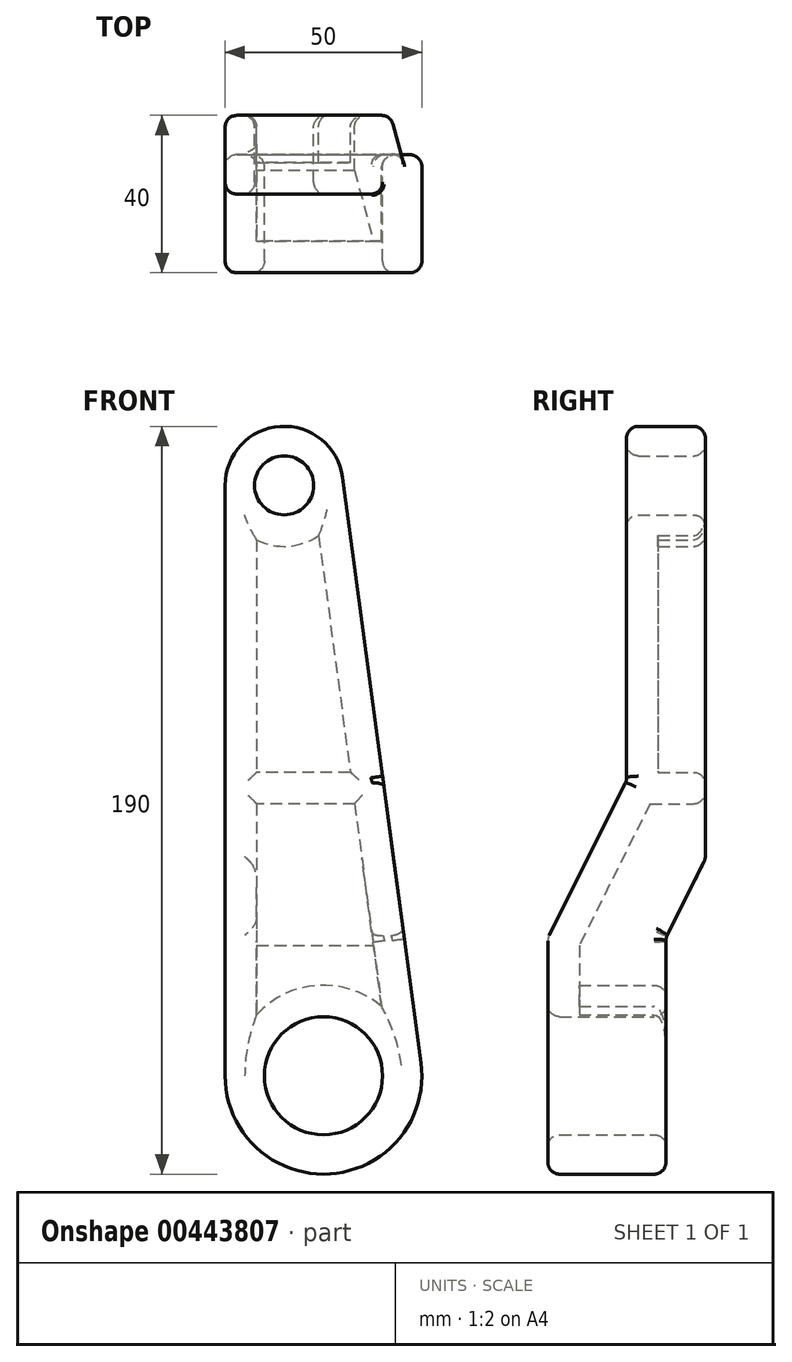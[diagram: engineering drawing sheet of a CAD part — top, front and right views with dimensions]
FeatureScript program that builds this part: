
annotation { "Feature Type Name" : "Feature", "Feature Type Description" : "" }
export const myFeature = defineFeature(function(context is Context, id is Id, definition is map)
    precondition{}
    {
        {
            var Q0;
            Q0=qCreatedBy(makeId("Front.planeOp"),FACE);
            var sketch = newSketch(context, id + "F0", { "sketchPlane" : qUnion([Q0])});
            skArc(sketch, "E0", {"start": v(-25, 0) * mm, "mid": v(1.66, -24.94) * mm, "end": v(24.78, 3.32) * mm});
            skArc(sketch, "E1", {"start": v(4.87, 152) * mm, "mid": v(-11, 164.97) * mm, "end": v(-25, 150) * mm});
            skLineSegment(sketch, "E2", {"start": v(-25, 150) * mm, "end": v(-25, 0) * mm});
            skLineSegment(sketch, "E3", {"start": v(4.87, 152) * mm, "end": v(24.78, 3.32) * mm});
            skSolve(sketch);
        }
        {
            var Q0;
            Q0 = qSketchRegion(id + "F0", true);
            extrude(context, id + "F1", {"entities" : qUnion([Q0]), "depth" : 40 * mm});
        }
        {
            var Q0;
            Q0=qCreatedBy(makeId("Right.planeOp"),FACE);
            var sketch = newSketch(context, id + "F2", { "sketchPlane" : qUnion([Q0])});
            skLineSegment(sketch, "E4", {"start": v(0, 0) * mm, "end": v(0, -25.94) * mm});
            skLineSegment(sketch, "E5", {"start": v(-10, -25.94) * mm, "end": v(-10, 35) * mm});
            skLineSegment(sketch, "E6", {"start": v(-10, 35) * mm, "end": v(0, 55) * mm});
            skLineSegment(sketch, "E7", {"start": v(0, 55) * mm, "end": v(0, -25.94) * mm});
            skLineSegment(sketch, "E8", {"start": v(-40, 35) * mm, "end": v(-40, 165.97) * mm});
            skLineSegment(sketch, "E9", {"start": v(-20, 165.97) * mm, "end": v(-20, 75) * mm});
            skLineSegment(sketch, "E10", {"start": v(-20, 75) * mm, "end": v(-40, 35) * mm});
            skLineSegment(sketch, "E11", {"start": v(0, -25.94) * mm, "end": v(-10, -25.94) * mm});
            skLineSegment(sketch, "E12", {"start": v(-20, 165.97) * mm, "end": v(-40, 165.97) * mm});
            skSolve(sketch);
        }
        {
            var Q0;
            Q0 = qSketchRegion(id + "F2", true);
            extrude(context, id + "F3", {"entities" : qUnion([Q0]), "operationType" : NewBodyOperationType.REMOVE, "endBound" : BoundingType.THROUGH_ALL, "oppositeDirection" : true, "depth" : 25 * mm, "hasSecondDirection" : true, "secondDirectionBound" : SecondDirectionBoundingType.THROUGH_ALL, "secondDirectionOppositeDirection" : false, "secondDirectionDepth" : 25 * mm});
        }
        {
            var Q0;
            Q0=makeQuery(id+"F1.opExtrude","CAP_FACE",FACE,{"disambiguationData":[OSD([sQuery(id+"F0.wireOp",EDGE,"E0"),sQuery(id+"F0.wireOp",EDGE,"E1"),sQuery(id+"F0.wireOp",EDGE,"E2"),sQuery(id+"F0.wireOp",EDGE,"E3")])],"isStart":true});
            var sketch = newSketch(context, id + "F4", { "sketchPlane" : qUnion([Q0])});
            skCircle(sketch, "E13", {"center": v(10, 150) * mm, "radius": 7.5 * mm});
            skCircle(sketch, "E14", {"center": v(0, 0) * mm, "radius": 15 * mm});
            skSolve(sketch);
        }
        {
            var Q0;
            Q0=makeQuery(id+"F4.imprint","IMPRINT",FACE,{"disambiguationData":[TD([[makeQuery(id+"F4.imprint","IMPRINT",EDGE,{"derivedFrom":sQuery(id+"F4.wireOp",EDGE,"E13")}),1.0]])]});
            var Q1;
            Q1=makeQuery(id+"F4.imprint","IMPRINT",FACE,{"disambiguationData":[TD([[makeQuery(id+"F4.imprint","IMPRINT",EDGE,{"derivedFrom":sQuery(id+"F4.wireOp",EDGE,"E14")}),1.0]])]});
            extrude(context, id + "F5", {"entities" : qUnion([Q0, Q1]), "operationType" : NewBodyOperationType.REMOVE, "endBound" : BoundingType.THROUGH_ALL, "oppositeDirection" : true, "depth" : 25 * mm});
        }
        {
            var Q0;
            Q0=makeQuery(id+"F1.opExtrude","CAP_FACE",FACE,{"disambiguationData":[OSD([sQuery(id+"F0.wireOp",EDGE,"E0"),sQuery(id+"F0.wireOp",EDGE,"E1"),sQuery(id+"F0.wireOp",EDGE,"E2"),sQuery(id+"F0.wireOp",EDGE,"E3")])],"isStart":true});
            var Q1;
            Q1=makeQuery(id+"F3.boolean.opBoolean","COPY",FACE,{"derivedFrom":makeQuery(id+"F3.opExtrude","SWEPT_FACE",FACE,{"disambiguationData":[OSD([sQuery(id+"F2.wireOp",EDGE,"E6")])]})});
            var Q2;
            Q2=makeQuery(id+"F3.boolean.opBoolean","COPY",FACE,{"derivedFrom":makeQuery(id+"F3.opExtrude","SWEPT_FACE",FACE,{"disambiguationData":[OSD([sQuery(id+"F2.wireOp",EDGE,"E5")])]})});
            shell(context, id + "F6", {"entities" : qUnion([Q0, Q1, Q2]), "thickness" : 8 * mm});
        }
        {
            var Q0;
            Q0=makeQuery(id+"F1.opExtrude","CAP_FACE",FACE,{"disambiguationData":[OSD([sQuery(id+"F0.wireOp",EDGE,"E0"),sQuery(id+"F0.wireOp",EDGE,"E1"),sQuery(id+"F0.wireOp",EDGE,"E2"),sQuery(id+"F0.wireOp",EDGE,"E3")])],"isStart":true});
            var sketch = newSketch(context, id + "F7", { "sketchPlane" : qUnion([Q0])});
            skLineSegment(sketch, "E15", {"start": v(-6.82, 77.11) * mm, "end": v(17, 77.11) * mm});
            skLineSegment(sketch, "E16", {"start": v(-7.9, 69.11) * mm, "end": v(17, 69.11) * mm});
            skLineSegment(sketch, "E17.0", {"start": v(1.23, 137.22) * mm, "end": v(-9.79, 55) * mm});
            skLineSegment(sketch, "E18.0", {"start": v(17, 136.17) * mm, "end": v(17, 55) * mm});
            skSolve(sketch);
        }
        {
            var Q0;
            Q0 = qSketchRegion(id + "F7", true);
            extrude(context, id + "F8", {"entities" : qUnion([Q0]), "operationType" : NewBodyOperationType.ADD, "endBound" : BoundingType.UP_TO_NEXT, "oppositeDirection" : true, "depth" : 25 * mm});
        }
        {
            var Q0;
            Q0=makeQuery(id+"F8.boolean.opBoolean","MERGE",FACE,{"derivedFrom":[makeQuery(id+"F1.opExtrude","CAP_FACE",FACE,{"disambiguationData":[OSD([sQuery(id+"F0.wireOp",EDGE,"E0"),sQuery(id+"F0.wireOp",EDGE,"E1"),sQuery(id+"F0.wireOp",EDGE,"E2"),sQuery(id+"F0.wireOp",EDGE,"E3")])],"isStart":true}),makeQuery(id+"F8.opExtrude","CAP_FACE",FACE,{"disambiguationData":[OSD([sQuery(id+"F7.wireOp",EDGE,"E15"),sQuery(id+"F7.wireOp",EDGE,"E16"),sQuery(id+"F7.wireOp",EDGE,"E17.0"),sQuery(id+"F7.wireOp",EDGE,"E18.0")])],"isStart":true})]});
            var Q1;
            Q1=makeQuery(id+"F6.opShell","OFFSET_FACE",FACE,{"disambiguationData":[OSD([sQuery(id+"F2.wireOp",EDGE,"E6")])]});
            var Q2;
            Q2=makeQuery(id+"F3.boolean.opBoolean","COPY",FACE,{"derivedFrom":makeQuery(id+"F3.opExtrude","SWEPT_FACE",FACE,{"disambiguationData":[OSD([sQuery(id+"F2.wireOp",EDGE,"E5")])]})});
            var Q3;
            Q3=makeQuery(id+"F3.boolean.opBoolean","INTERSECT",EDGE,{"derivedFrom":[makeQuery(id+"F1.opExtrude","SWEPT_FACE",FACE,{"disambiguationData":[OSD([sQuery(id+"F0.wireOp",EDGE,"E2")])]}),makeQuery(id+"F3.opExtrude","SWEPT_FACE",FACE,{"disambiguationData":[OSD([sQuery(id+"F2.wireOp",EDGE,"E6")])]})]});
            var Q4;
            Q4=makeQuery(id+"F3.boolean.opBoolean","COPY",FACE,{"derivedFrom":makeQuery(id+"F3.opExtrude","SWEPT_FACE",FACE,{"disambiguationData":[OSD([sQuery(id+"F2.wireOp",EDGE,"E9")])]})});
            var Q5;
            Q5=makeQuery(id+"F3.boolean.opBoolean","COPY",FACE,{"derivedFrom":makeQuery(id+"F3.opExtrude","SWEPT_FACE",FACE,{"disambiguationData":[OSD([sQuery(id+"F2.wireOp",EDGE,"E10")])]})});
            var Q6;
            Q6=makeQuery(id+"F1.opExtrude","CAP_FACE",FACE,{"disambiguationData":[OSD([sQuery(id+"F0.wireOp",EDGE,"E0"),sQuery(id+"F0.wireOp",EDGE,"E1"),sQuery(id+"F0.wireOp",EDGE,"E2"),sQuery(id+"F0.wireOp",EDGE,"E3")])],"isStart":false});
            fillet(context, id + "F9", {"entities" : qUnion([Q0, Q1, Q2, Q3, Q4, Q5, Q6]), "radius" : 3 * mm, "tangentPropagation" : true, "allowEdgeOverflow" : false});
        }
    });
